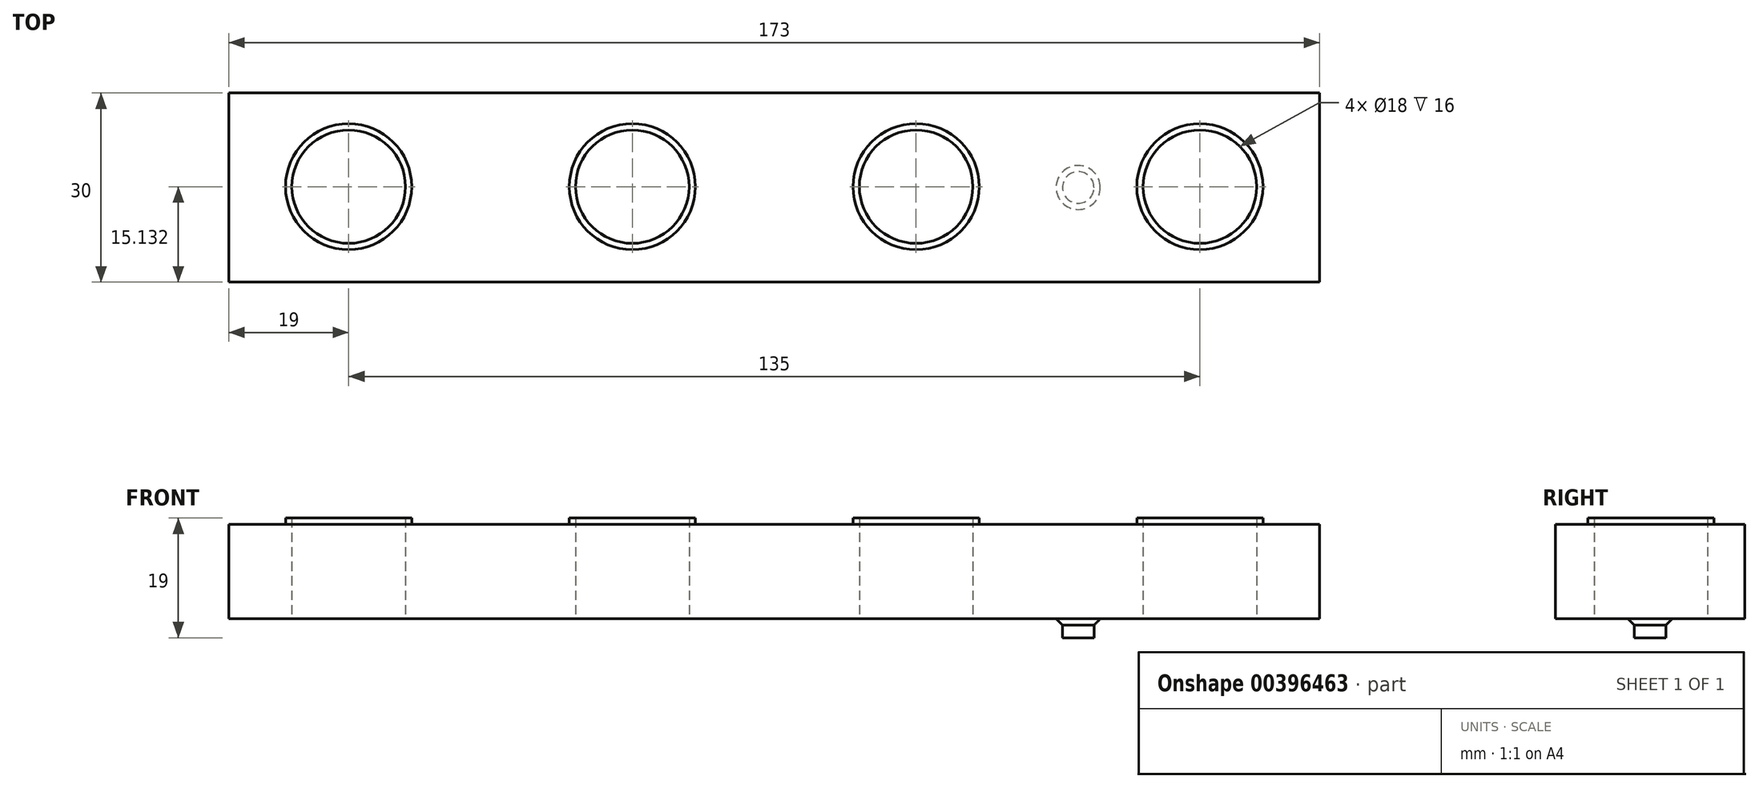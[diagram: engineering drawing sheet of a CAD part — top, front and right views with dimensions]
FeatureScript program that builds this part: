
annotation { "Feature Type Name" : "Feature", "Feature Type Description" : "" }
export const myFeature = defineFeature(function(context is Context, id is Id, definition is map)
    precondition{}
    {
        {
            var Q0;
            Q0=qCreatedBy(makeId("Top.planeOp"),FACE);
            var sketch = newSketch(context, id + "F0", { "sketchPlane" : qUnion([Q0])});
            skLineSegment(sketch, "E0.bottom", {"start": v(86.5, -15) * mm, "end": v(-86.5, -15) * mm});
            skLineSegment(sketch, "E0.top", {"start": v(86.5, 15) * mm, "end": v(-86.5, 15) * mm});
            skLineSegment(sketch, "E0.left", {"start": v(86.5, -15) * mm, "end": v(86.5, 15) * mm});
            skLineSegment(sketch, "E0.right", {"start": v(-86.5, -15) * mm, "end": v(-86.5, 15) * mm});
            skPoint(sketch, "E0.middle", {"position": v(0, 0) * mm});
            skLineSegment(sketch, "E1", {"start": v(-86.5, 0) * mm, "end": v(86.5, 0) * mm, "construction": true});
            skLineSegment(sketch, "E2", {"start": v(0, 15) * mm, "end": v(0, -15) * mm, "construction": true});
            skSolve(sketch);
        }
        {
            var Q0;
            Q0=makeQuery(id+"F0.imprint","IMPRINT",FACE,{"disambiguationData":[TD([[makeQuery(id+"F0.imprint","IMPRINT",EDGE,{"derivedFrom":sQuery(id+"F0.wireOp",EDGE,"E0.bottom")}),-1.0]])]});
            extrude(context, id + "F1", {"entities" : qUnion([Q0]), "oppositeDirection" : true, "depth" : 3 * mm});
        }
        {
            var Q0;
            Q0=makeQuery(id+"F0.imprint","IMPRINT",FACE,{"disambiguationData":[TD([[makeQuery(id+"F0.imprint","IMPRINT",EDGE,{"derivedFrom":sQuery(id+"F0.wireOp",EDGE,"E0.bottom")}),-1.0]])]});
            var sketch = newSketch(context, id + "F2", { "sketchPlane" : qUnion([Q0])});
            skCircle(sketch, "E3.MirrorC", {"center": v(-67.5, 0.13) * mm, "radius": 9 * mm});
            skCircle(sketch, "E4.1.0.0", {"center": v(-22.5, 0.13) * mm, "radius": 9 * mm});
            skCircle(sketch, "E4.2.0.0", {"center": v(22.5, 0.13) * mm, "radius": 9 * mm});
            skCircle(sketch, "E4.3.0.0", {"center": v(67.5, 0.13) * mm, "radius": 9 * mm});
            skLineSegment(sketch, "E4.direction1", {"start": v(-67.5, 0.13) * mm, "end": v(-22.5, 0.13) * mm, "construction": true});
            skSolve(sketch);
        }
        {
            var Q0;
            Q0=makeQuery(id+"F2.imprint","IMPRINT",FACE,{"disambiguationData":[TD([[makeQuery(id+"F2.imprint","IMPRINT",EDGE,{"derivedFrom":sQuery(id+"F2.wireOp",EDGE,"E3.MirrorC")}),-1.0]])]});
            var Q1;
            Q1=makeQuery(id+"F2.imprint","IMPRINT",FACE,{"disambiguationData":[TD([[makeQuery(id+"F2.imprint","IMPRINT",EDGE,{"derivedFrom":sQuery(id+"F2.wireOp",EDGE,"E4.1.0.0")}),-1.0]])]});
            var Q2;
            Q2=makeQuery(id+"F2.imprint","IMPRINT",FACE,{"disambiguationData":[TD([[makeQuery(id+"F2.imprint","IMPRINT",EDGE,{"derivedFrom":sQuery(id+"F2.wireOp",EDGE,"E4.2.0.0")}),-1.0]])]});
            var Q3;
            Q3=makeQuery(id+"F2.imprint","IMPRINT",FACE,{"disambiguationData":[TD([[makeQuery(id+"F2.imprint","IMPRINT",EDGE,{"derivedFrom":sQuery(id+"F2.wireOp",EDGE,"E4.3.0.0")}),-1.0]])]});
            var Q4;
            Q4=sQuery(id+"F2.wireOp",EDGE,"297f3a6d-45f4-47e1-9aab-aaa11929158c0.MirrorC");
            var Q5;
            Q5=sQuery(id+"F2.wireOp",EDGE,"E3.MirrorC");
            var Q6;
            Q6=sQuery(id+"F2.wireOp",EDGE,"297f3a6d-45f4-47e1-9aab-aaa11929158c2.MirrorC");
            var Q7;
            Q7=sQuery(id+"F2.wireOp",EDGE,"11a5fd5d-dd43-4bd8-b7f0-a4588dbfd579.1.0.0");
            var Q8;
            Q8=sQuery(id+"F2.wireOp",EDGE,"11a5fd5d-dd43-4bd8-b7f0-a4588dbfd579.2.0.0");
            extrude(context, id + "F3", {"entities" : qUnion([Q0, Q1, Q2, Q3]), "operationType" : NewBodyOperationType.ADD, "surfaceEntities" : qUnion([Q4, Q5, Q6, Q7, Q8]), "depth" : 15 * mm});
        }
        {
            var Q0;
            Q0=makeQuery(id+"F0.imprint","IMPRINT",FACE,{"disambiguationData":[TD([[makeQuery(id+"F0.imprint","IMPRINT",EDGE,{"derivedFrom":sQuery(id+"F0.wireOp",EDGE,"E0.bottom")}),-1.0]])]});
            var sketch = newSketch(context, id + "F4", { "sketchPlane" : qUnion([Q0])});
            skLineSegment(sketch, "E5", {"start": v(-48.2, 15.5) * mm, "end": v(-48.2, -15.5) * mm, "construction": true});
            skCircle(sketch, "E6", {"center": v(-48.2, 0) * mm, "radius": 2.5 * mm});
            skCircle(sketch, "E7.MirrorC", {"center": v(48.2, 0) * mm, "radius": 2.5 * mm});
            skSolve(sketch);
        }
        {
            var Q0;
            Q0=makeQuery(id+"F4.imprint","IMPRINT",FACE,{"disambiguationData":[TD([[makeQuery(id+"F4.imprint","IMPRINT",EDGE,{"derivedFrom":sQuery(id+"F4.wireOp",EDGE,"E6")}),1.0]])]});
            var Q1;
            Q1=makeQuery(id+"F4.imprint","IMPRINT",FACE,{"disambiguationData":[TD([[makeQuery(id+"F4.imprint","IMPRINT",EDGE,{"derivedFrom":sQuery(id+"F4.wireOp",EDGE,"E7.MirrorC")}),-1.0]])]});
            var Q2;
            Q2=sQuery(id+"F4.wireOp",EDGE,"E6");
            var Q3;
            Q3=sQuery(id+"F4.wireOp",EDGE,"E7.MirrorC");
            extrude(context, id + "F5", {"entities" : qUnion([Q0, Q1]), "operationType" : NewBodyOperationType.REMOVE, "surfaceEntities" : qUnion([Q2, Q3]), "oppositeDirection" : true, "depth" : 25 * mm});
        }
        {
            var Q0;
            Q0=makeQuery(id+"F5.boolean.opBoolean","COPY",EDGE,{"derivedFrom":makeQuery(id+"F5.opExtrude","CAP_EDGE",EDGE,{"disambiguationData":[OSD([sQuery(id+"F4.wireOp",EDGE,"E6")])],"isStart":true})});
            var Q1;
            Q1=makeQuery(id+"F5.boolean.opBoolean","COPY",EDGE,{"derivedFrom":makeQuery(id+"F5.opExtrude","CAP_EDGE",EDGE,{"disambiguationData":[OSD([sQuery(id+"F4.wireOp",EDGE,"E7.MirrorC")])],"isStart":true})});
            chamfer(context, id + "F6", {"entities" : qUnion([Q0, Q1]), "width" : 1 * mm, "tangentPropagation" : true});
        }
        {
            var Q0;
            Q0=makeQuery(id+"F3.opExtrude","CAP_FACE",FACE,{"disambiguationData":[OSD([sQuery(id+"F2.wireOp",EDGE,"E3.MirrorC")])],"isStart":false});
            var sketch = newSketch(context, id + "F7", { "sketchPlane" : qUnion([Q0])});
            skCircle(sketch, "E8", {"center": v(-67.5, 0.13) * mm, "radius": 10 * mm});
            skCircle(sketch, "E9.1.0.0", {"center": v(-22.5, 0.13) * mm, "radius": 10 * mm});
            skCircle(sketch, "E9.2.0.0", {"center": v(22.5, 0.13) * mm, "radius": 10 * mm});
            skCircle(sketch, "E9.3.0.0", {"center": v(67.5, 0.13) * mm, "radius": 10 * mm});
            skLineSegment(sketch, "E9.direction1", {"start": v(-67.5, 0.13) * mm, "end": v(-22.5, 0.13) * mm, "construction": true});
            skSolve(sketch);
        }
        {
            var Q0;
            Q0=makeQuery(id+"F7.imprint","IMPRINT",FACE,{"disambiguationData":[TD([[makeQuery(id+"F7.imprint","IMPRINT",EDGE,{"derivedFrom":sQuery(id+"F7.wireOp",EDGE,"E9.1.0.0")}),1.0]])]});
            var Q1;
            Q1=makeQuery(id+"F7.imprint","IMPRINT",FACE,{"disambiguationData":[TD([[makeQuery(id+"F7.imprint","IMPRINT",EDGE,{"derivedFrom":sQuery(id+"F7.wireOp",EDGE,"E9.2.0.0")}),1.0]])]});
            var Q2;
            Q2=makeQuery(id+"F7.imprint","IMPRINT",FACE,{"disambiguationData":[TD([[makeQuery(id+"F7.imprint","IMPRINT",EDGE,{"derivedFrom":sQuery(id+"F7.wireOp",EDGE,"E9.3.0.0")}),1.0]])]});
            var Q3;
            Q3=makeQuery(id+"F7.imprint","IMPRINT",FACE,{"disambiguationData":[TD([[makeQuery(id+"F7.imprint","IMPRINT",EDGE,{"derivedFrom":makeQuery(id+"F3.opExtrude","CAP_EDGE",EDGE,{"disambiguationData":[OSD([sQuery(id+"F2.wireOp",EDGE,"E3.MirrorC")])],"isStart":false})}),-1.0]])]});
            var Q4;
            Q4=makeQuery(id+"F7.imprint","IMPRINT",FACE,{"disambiguationData":[TD([[makeQuery(id+"F7.imprint","IMPRINT",EDGE,{"derivedFrom":sQuery(id+"F7.wireOp",EDGE,"E8")}),1.0]])]});
            var Q5;
            Q5=sQuery(id+"F7.wireOp",EDGE,"E8");
            var Q6;
            Q6=sQuery(id+"F7.wireOp",EDGE,"E9.1.0.0");
            var Q7;
            Q7=sQuery(id+"F7.wireOp",EDGE,"E9.2.0.0");
            var Q8;
            Q8=sQuery(id+"F7.wireOp",EDGE,"E9.3.0.0");
            extrude(context, id + "F8", {"entities" : qUnion([Q0, Q1, Q2, Q3, Q4]), "operationType" : NewBodyOperationType.ADD, "surfaceEntities" : qUnion([Q5, Q6, Q7, Q8]), "endBound" : BoundingType.SYMMETRIC, "depth" : 2 * mm});
        }
    });
